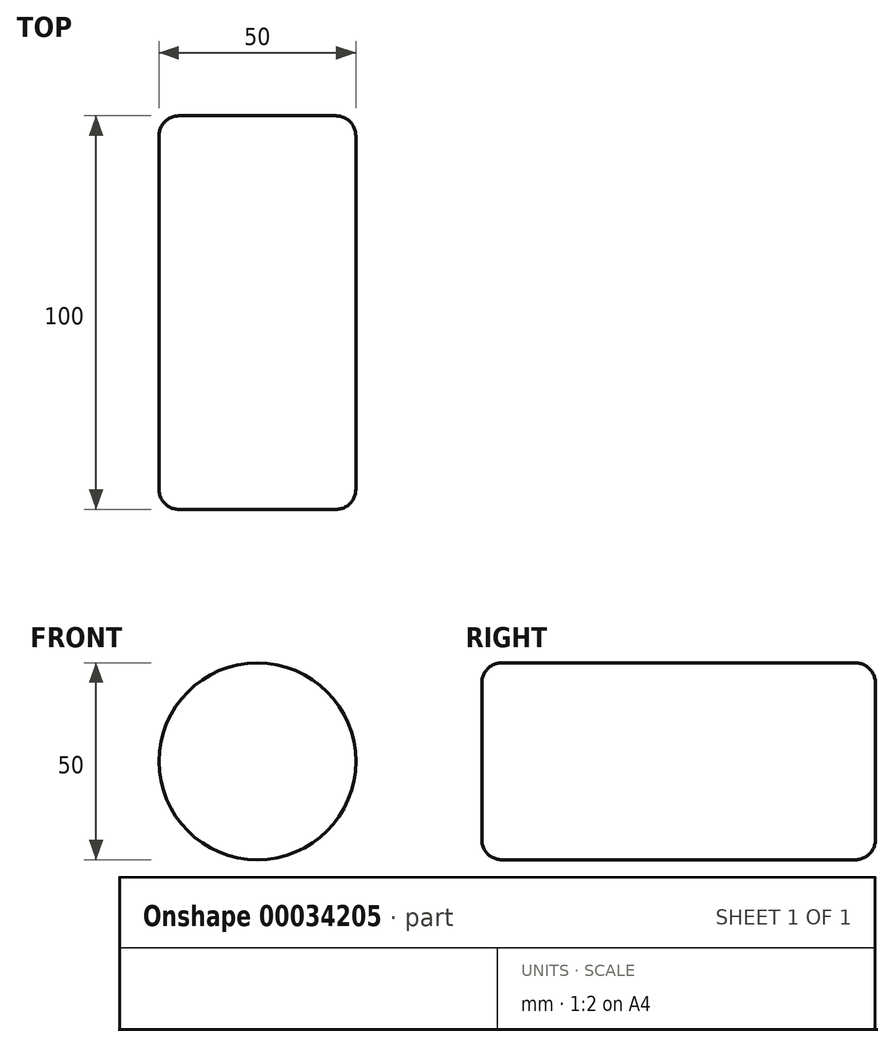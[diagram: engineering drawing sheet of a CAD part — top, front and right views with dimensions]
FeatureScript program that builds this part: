
annotation { "Feature Type Name" : "Feature", "Feature Type Description" : "" }
export const myFeature = defineFeature(function(context is Context, id is Id, definition is map)
    precondition{}
    {
        {
            var Q0;
            Q0=qCreatedBy(makeId("Front.planeOp"),FACE);
            var sketch = newSketch(context, id + "F0", { "sketchPlane" : qUnion([Q0])});
            skCircle(sketch, "E0", {"center": v(0, 0) * mm, "radius": 25 * mm});
            skSolve(sketch);
        }
        {
            var Q0;
            Q0 = qSketchRegion(id + "F0", true);
            extrude(context, id + "F1", {"entities" : qUnion([Q0]), "endBound" : BoundingType.SYMMETRIC, "depth" : 100 * mm});
        }
        {
            var Q0;
            Q0=makeQuery(id+"F1.opExtrude","CAP_FACE",FACE,{"disambiguationData":[OSD([sQuery(id+"F0.wireOp",EDGE,"E0")])],"isStart":false});
            var Q1;
            Q1=makeQuery(id+"F1.opExtrude","SWEPT_FACE",FACE,{"disambiguationData":[OSD([sQuery(id+"F0.wireOp",EDGE,"E0")])]});
            fillet(context, id + "F2", {"entities" : qUnion([Q0, Q1]), "radius" : 5.08 * mm, "tangentPropagation" : true, "allowEdgeOverflow" : false});
        }
    });
